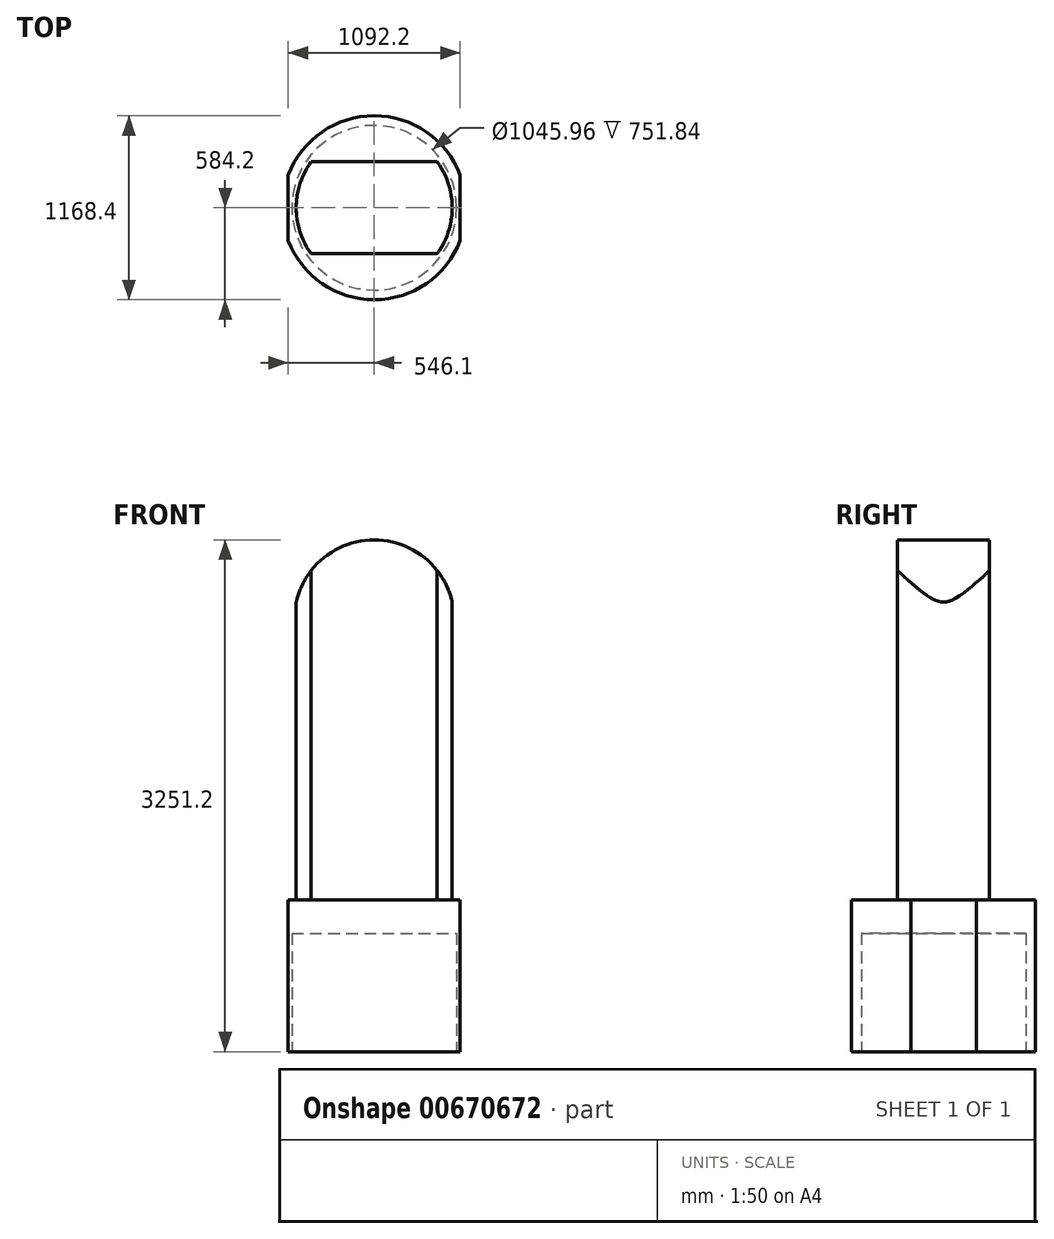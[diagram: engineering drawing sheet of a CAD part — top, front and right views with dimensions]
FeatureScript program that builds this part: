
annotation { "Feature Type Name" : "Feature", "Feature Type Description" : "" }
export const myFeature = defineFeature(function(context is Context, id is Id, definition is map)
    precondition{}
    {
        {
            var Q0;
            Q0=qCreatedBy(makeId("Top.planeOp"),FACE);
            var sketch = newSketch(context, id + "F0", { "sketchPlane" : qUnion([Q0])});
            skCircle(sketch, "E0", {"center": v(0, 0) * mm, "radius": 584.2 * mm});
            skLineSegment(sketch, "E1", {"start": v(-546.1, 207.52) * mm, "end": v(-546.1, -207.52) * mm});
            skLineSegment(sketch, "E2.MirrorCS", {"start": v(546.1, 207.52) * mm, "end": v(546.1, -207.52) * mm});
            skSolve(sketch);
        }
        {
            var Q0;
            {var subQ0=sQuery(id+"F0.wireOp",EDGE,"E1");Q0=makeQuery(id+"F0.imprint","IMPRINT",FACE,{"disambiguationData":[TD([[makeQuery(id+"F0.imprint","IMPRINT",EDGE,{"derivedFrom":subQ0}),1.0]])]});}
            extrude(context, id + "F1", {"entities" : qUnion([Q0]), "depth" : 965.2 * mm, "offsetDistance" : 25.4 * mm});
        }
        {
            var Q0;
            Q0=makeQuery(id+"F1.opExtrude","CAP_FACE",FACE,{"disambiguationData":[OSD([sQuery(id+"F0.wireOp",EDGE,"E0"),sQuery(id+"F0.wireOp",EDGE,"E1"),sQuery(id+"F0.wireOp",EDGE,"E2.MirrorCS")])],"isStart":false});
            var sketch = newSketch(context, id + "F2", { "sketchPlane" : qUnion([Q0])});
            skCircle(sketch, "E3", {"center": v(0, 0) * mm, "radius": 495.3 * mm});
            skLineSegment(sketch, "E4", {"start": v(400, 292.1) * mm, "end": v(-400, 292.1) * mm});
            skLineSegment(sketch, "E5.MirrorCS", {"start": v(400, -292.1) * mm, "end": v(-400, -292.1) * mm});
            skSolve(sketch);
        }
        {
            var Q0;
            {var subQ0=sQuery(id+"F2.wireOp",EDGE,"E4");Q0=makeQuery(id+"F2.imprint","IMPRINT",FACE,{"disambiguationData":[TD([[makeQuery(id+"F2.imprint","IMPRINT",EDGE,{"derivedFrom":subQ0}),1.0]])]});}
            extrude(context, id + "F3", {"entities" : qUnion([Q0]), "operationType" : NewBodyOperationType.ADD, "depth" : 2362.2 * mm, "offsetDistance" : 25.4 * mm});
        }
        {
            var Q0;
            Q0=makeQuery(id+"F3.opExtrude","SWEPT_FACE",FACE,{"disambiguationData":[OSD([sQuery(id+"F2.wireOp",EDGE,"E5.MirrorCS")])]});
            var sketch = newSketch(context, id + "F4", { "sketchPlane" : qUnion([Q0])});
            skCircle(sketch, "E6", {"center": v(0, 2743.2) * mm, "radius": 508 * mm});
            skLineSegment(sketch, "E7", {"start": v(-506.02, 2788.06) * mm, "end": v(-619.61, 3534.23) * mm});
            skLineSegment(sketch, "E8", {"start": v(507.93, 2734.65) * mm, "end": v(693.92, 3608.87) * mm});
            skLineSegment(sketch, "E9", {"start": v(-619.61, 3534.23) * mm, "end": v(693.92, 3608.87) * mm});
            skSolve(sketch);
        }
        {
            var Q0;
            {var subQ6=sQuery(id+"F4.wireOp",EDGE,"E7");Q0=makeQuery(id+"F4.imprint","IMPRINT",FACE,{"disambiguationData":[TD([[makeQuery(id+"F4.imprint","IMPRINT",EDGE,{"derivedFrom":subQ6}),-1.0]])]});}
            var Q1;
            {var subQ1=sQuery(id+"F2.wireOp",EDGE,"E5.MirrorCS");var subQ7=makeQuery(id+"F3.opExtrude","CAP_EDGE",EDGE,{"disambiguationData":[OSD([subQ1])],"isStart":false});Q1=makeQuery(id+"F4.imprint","IMPRINT",FACE,{"disambiguationData":[TD([[makeQuery(id+"F4.imprint","IMPRINT",EDGE,{"derivedFrom":subQ7}),1.0]])]});}
            extrude(context, id + "F5", {"entities" : qUnion([Q0, Q1]), "operationType" : NewBodyOperationType.REMOVE, "oppositeDirection" : true, "depth" : 1524 * mm, "offsetDistance" : 25.4 * mm});
        }
        {
            var Q0;
            Q0=makeQuery(id+"F1.opExtrude","CAP_FACE",FACE,{"disambiguationData":[OSD([sQuery(id+"F0.wireOp",EDGE,"E0"),sQuery(id+"F0.wireOp",EDGE,"E1"),sQuery(id+"F0.wireOp",EDGE,"E2.MirrorCS")])],"isStart":true});
            var sketch = newSketch(context, id + "F6", { "sketchPlane" : qUnion([Q0])});
            skCircle(sketch, "E10", {"center": v(0, 0) * mm, "radius": 522.98 * mm});
            skSolve(sketch);
        }
        {
            var Q0;
            Q0=makeQuery(id+"F6.imprint","IMPRINT",FACE,{"disambiguationData":[TD([[makeQuery(id+"F6.imprint","IMPRINT",EDGE,{"derivedFrom":sQuery(id+"F6.wireOp",EDGE,"E10")}),1.0]])]});
            extrude(context, id + "F7", {"entities" : qUnion([Q0]), "operationType" : NewBodyOperationType.REMOVE, "oppositeDirection" : true, "depth" : 751.84 * mm, "offsetDistance" : 25.4 * mm});
        }
    });
